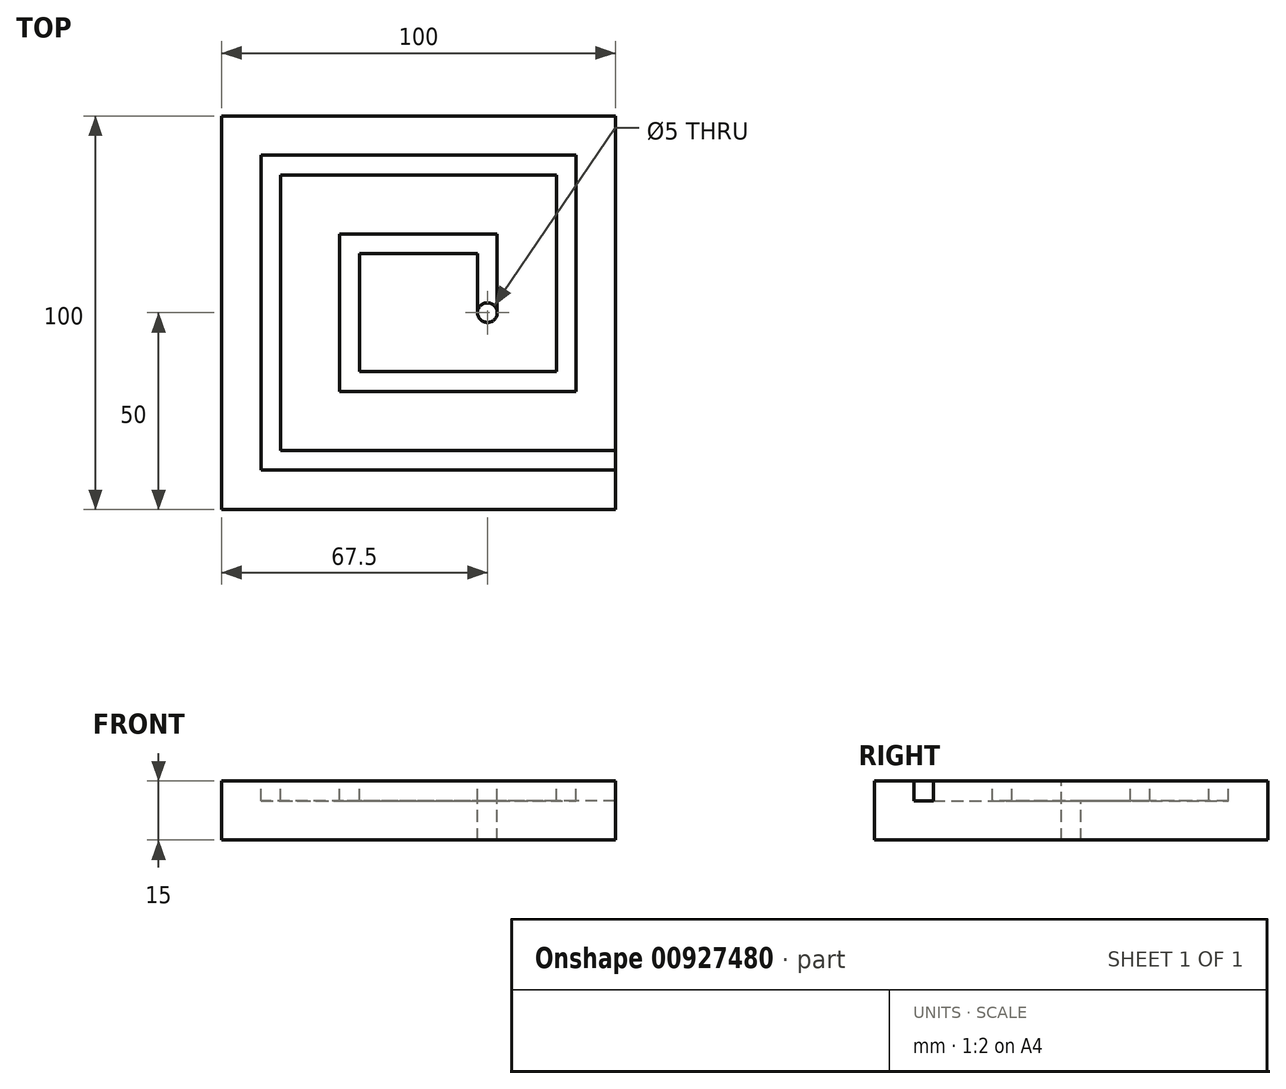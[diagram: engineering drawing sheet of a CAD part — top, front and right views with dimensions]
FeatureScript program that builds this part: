
annotation { "Feature Type Name" : "Feature", "Feature Type Description" : "" }
export const myFeature = defineFeature(function(context is Context, id is Id, definition is map)
    precondition{}
    {
        {
            var Q0;
            Q0=qCreatedBy(makeId("Top.planeOp"),FACE);
            var sketch = newSketch(context, id + "F0", { "sketchPlane" : qUnion([Q0])});
            skLineSegment(sketch, "E0.bottom", {"start": v(50, -50) * mm, "end": v(-50, -50) * mm});
            skLineSegment(sketch, "E0.top", {"start": v(50, 50) * mm, "end": v(-50, 50) * mm});
            skLineSegment(sketch, "E0.left", {"start": v(50, -50) * mm, "end": v(50, 50) * mm});
            skLineSegment(sketch, "E0.right", {"start": v(-50, -50) * mm, "end": v(-50, 50) * mm});
            skPoint(sketch, "E0.middle", {"position": v(0, 0) * mm});
            skSolve(sketch);
        }
        {
            var Q0;
            Q0=makeQuery(id+"F0.imprint","IMPRINT",FACE,{"disambiguationData":[TD([[makeQuery(id+"F0.imprint","IMPRINT",EDGE,{"derivedFrom":sQuery(id+"F0.wireOp",EDGE,"E0.bottom")}),-1.0]])]});
            extrude(context, id + "F1", {"entities" : qUnion([Q0]), "depth" : 15 * mm, "offsetDistance" : 25 * mm});
        }
        {
            var Q0;
            Q0=makeQuery(id+"F1.opExtrude","CAP_FACE",FACE,{"disambiguationData":[OSD([sQuery(id+"F0.wireOp",EDGE,"E0.bottom"),sQuery(id+"F0.wireOp",EDGE,"E0.top"),sQuery(id+"F0.wireOp",EDGE,"E0.left"),sQuery(id+"F0.wireOp",EDGE,"E0.right")])],"isStart":false});
            var sketch = newSketch(context, id + "F2", { "sketchPlane" : qUnion([Q0])});
            skLineSegment(sketch, "E1", {"start": v(50, -40) * mm, "end": v(-40, -40) * mm});
            skLineSegment(sketch, "E2", {"start": v(-40, -40) * mm, "end": v(-40, 40) * mm});
            skLineSegment(sketch, "E3", {"start": v(-40, 40) * mm, "end": v(40, 40) * mm});
            skLineSegment(sketch, "E4", {"start": v(40, 40) * mm, "end": v(40, -20) * mm});
            skLineSegment(sketch, "E5", {"start": v(40, -20) * mm, "end": v(-20, -20) * mm});
            skLineSegment(sketch, "E6", {"start": v(-20, -20) * mm, "end": v(-20, 20) * mm});
            skLineSegment(sketch, "E7", {"start": v(-20, 20) * mm, "end": v(20, 20) * mm});
            skLineSegment(sketch, "E8", {"start": v(20, 20) * mm, "end": v(20, 0) * mm});
            skLineSegment(sketch, "E9.0", {"start": v(15, 15) * mm, "end": v(15, 0) * mm});
            skLineSegment(sketch, "E9.1", {"start": v(-15, 15) * mm, "end": v(15, 15) * mm});
            skLineSegment(sketch, "E9.2", {"start": v(-15, -15) * mm, "end": v(-15, 15) * mm});
            skLineSegment(sketch, "E9.3", {"start": v(35, -15) * mm, "end": v(-15, -15) * mm});
            skLineSegment(sketch, "E9.4", {"start": v(50, -35) * mm, "end": v(-35, -35) * mm});
            skLineSegment(sketch, "E9.5", {"start": v(-35, -35) * mm, "end": v(-35, 35) * mm});
            skLineSegment(sketch, "E9.6", {"start": v(-35, 35) * mm, "end": v(35, 35) * mm});
            skLineSegment(sketch, "E9.7", {"start": v(35, 35) * mm, "end": v(35, -15) * mm});
            skLineSegment(sketch, "E10", {"start": v(15, 0) * mm, "end": v(20, 0) * mm});
            skLineSegment(sketch, "E11", {"start": v(50, -35) * mm, "end": v(50, -40) * mm});
            skSolve(sketch);
        }
        {
            var Q0;
            Q0 = qSketchRegion(id + "F2", true);
            extrude(context, id + "F3", {"entities" : qUnion([Q0]), "operationType" : NewBodyOperationType.REMOVE, "oppositeDirection" : true, "depth" : 5 * mm, "offsetDistance" : 25 * mm});
        }
        {
            var Q0;
            Q0=makeQuery(id+"F1.opExtrude","CAP_FACE",FACE,{"disambiguationData":[OSD([sQuery(id+"F0.wireOp",EDGE,"E0.bottom"),sQuery(id+"F0.wireOp",EDGE,"E0.top"),sQuery(id+"F0.wireOp",EDGE,"E0.left"),sQuery(id+"F0.wireOp",EDGE,"E0.right")])],"isStart":false});
            var sketch = newSketch(context, id + "F4", { "sketchPlane" : qUnion([Q0])});
            skCircle(sketch, "E12", {"center": v(17.5, 0) * mm, "radius": 2.5 * mm});
            skSolve(sketch);
        }
        {
            var Q0;
            Q0 = qSketchRegion(id + "F4", true);
            extrude(context, id + "F5", {"entities" : qUnion([Q0]), "operationType" : NewBodyOperationType.REMOVE, "endBound" : BoundingType.UP_TO_NEXT, "oppositeDirection" : true, "depth" : 25 * mm, "offsetDistance" : 25 * mm});
        }
    });
